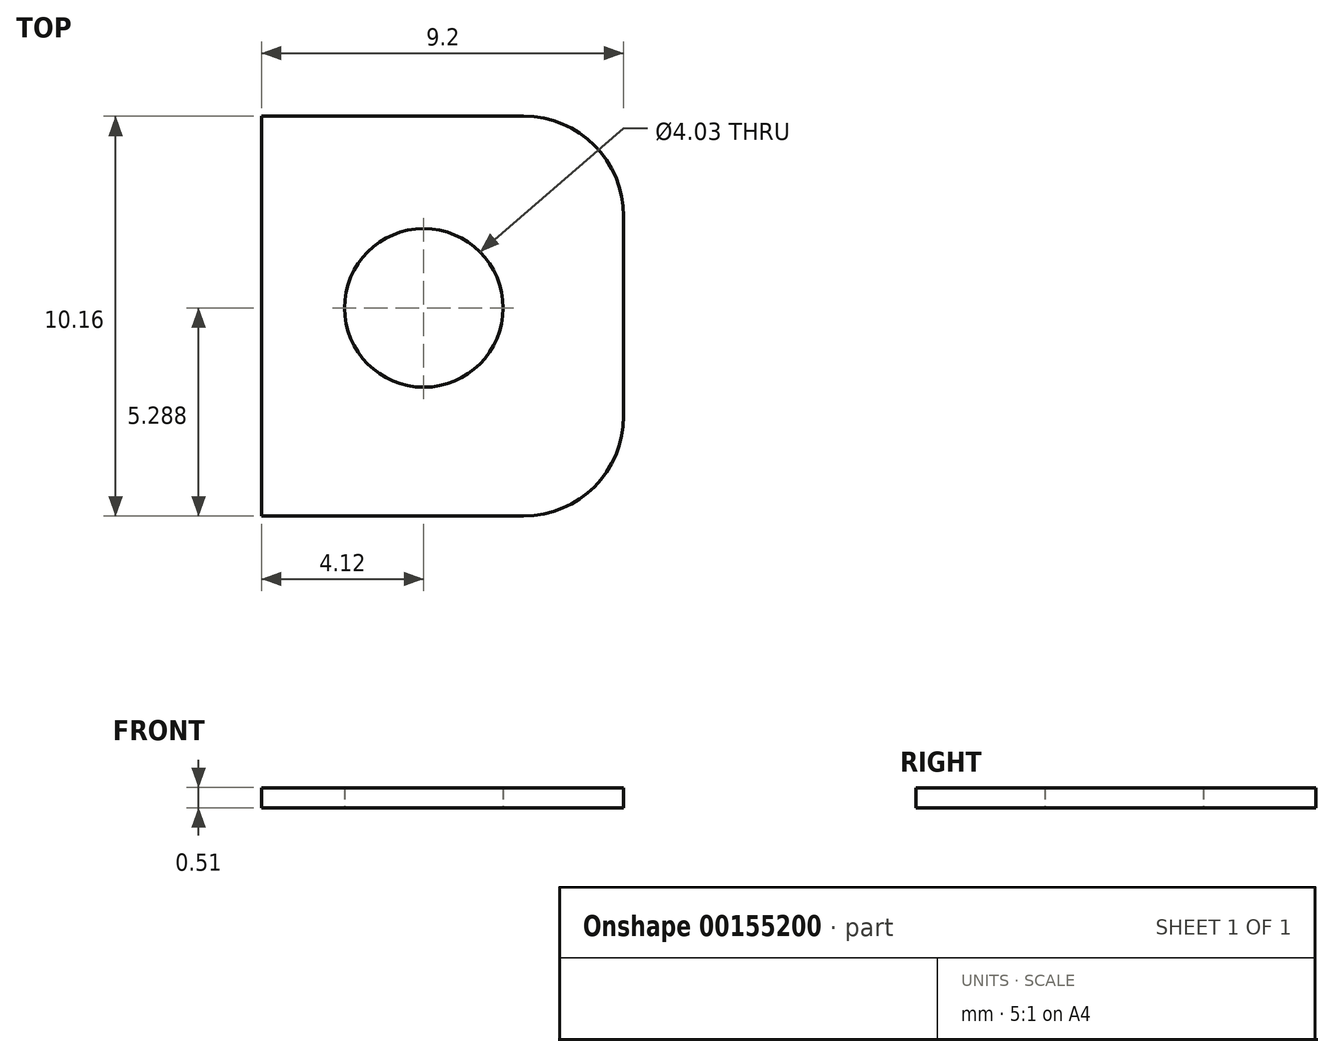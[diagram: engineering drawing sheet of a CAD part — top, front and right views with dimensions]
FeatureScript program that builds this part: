
annotation { "Feature Type Name" : "Feature", "Feature Type Description" : "" }
export const myFeature = defineFeature(function(context is Context, id is Id, definition is map)
    precondition{}
    {
        {
            var Q0;
            Q0=qCreatedBy(makeId("Top.planeOp"),FACE);
            var sketch = newSketch(context, id + "F0", { "sketchPlane" : qUnion([Q0])});
            skLineSegment(sketch, "E0", {"start": v(-3.64, 9.94) * mm, "end": v(5.08, 9.94) * mm});
            skLineSegment(sketch, "E1", {"start": v(5.08, 9.94) * mm, "end": v(5.08, -0.22) * mm});
            skLineSegment(sketch, "E2", {"start": v(5.08, -0.22) * mm, "end": v(-4.12, -0.22) * mm});
            skLineSegment(sketch, "E3", {"start": v(-4.12, -0.22) * mm, "end": v(-4.12, 9.94) * mm});
            skLineSegment(sketch, "E4", {"start": v(-4.12, 9.94) * mm, "end": v(-3.64, 9.94) * mm});
            skCircle(sketch, "E5", {"center": v(0, 5.07) * mm, "radius": 2.01 * mm});
            skSolve(sketch);
        }
        {
            var Q0;
            Q0=makeQuery(id+"F0.imprint","IMPRINT",FACE,{"disambiguationData":[TD([[makeQuery(id+"F0.imprint","IMPRINT",EDGE,{"derivedFrom":sQuery(id+"F0.wireOp",EDGE,"E0")}),-1.0]])]});
            extrude(context, id + "F1", {"entities" : qUnion([Q0]), "depth" : 0.5 * mm});
        }
        {
            var Q0;
            Q0=makeQuery(id+"F1.opExtrude","SWEPT_EDGE",EDGE,{"disambiguationData":[OSD([sQuery(id+"F0.wireOp",EDGE,"E0"),sQuery(id+"F0.wireOp",EDGE,"E1")])]});
            var Q1;
            Q1=makeQuery(id+"F1.opExtrude","SWEPT_EDGE",EDGE,{"disambiguationData":[OSD([sQuery(id+"F0.wireOp",EDGE,"E1"),sQuery(id+"F0.wireOp",EDGE,"E2")])]});
            fillet(context, id + "F2", {"entities" : qUnion([Q0, Q1]), "radius" : 2.54 * mm, "tangentPropagation" : true, "allowEdgeOverflow" : false});
        }
    });
